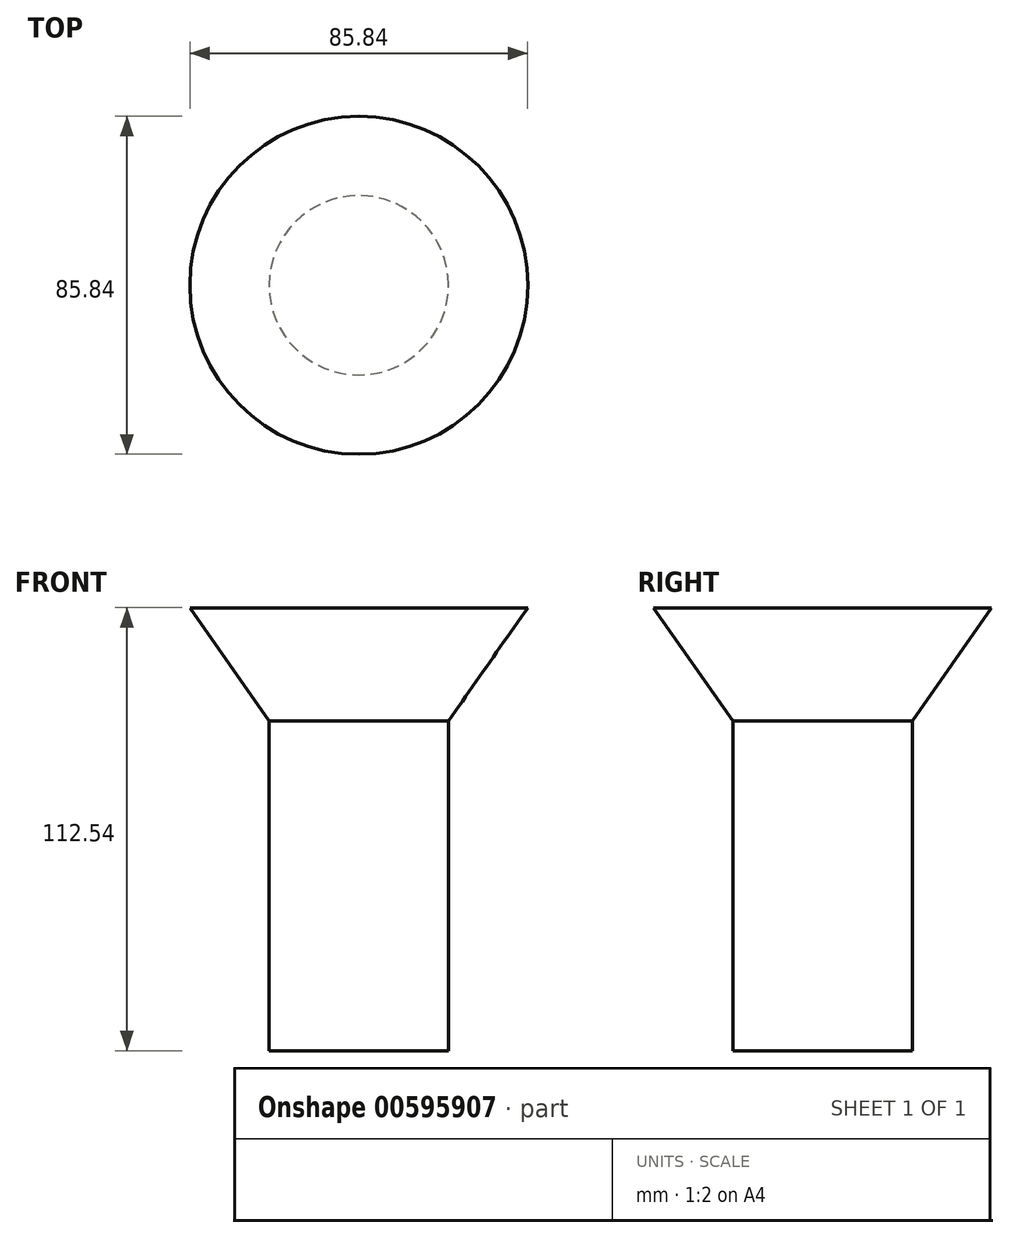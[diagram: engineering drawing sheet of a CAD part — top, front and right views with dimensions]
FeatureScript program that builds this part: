
annotation { "Feature Type Name" : "Feature", "Feature Type Description" : "" }
export const myFeature = defineFeature(function(context is Context, id is Id, definition is map)
    precondition{}
    {
        {
            var Q0;
            Q0=qCreatedBy(makeId("Right.planeOp"),FACE);
            var sketch = newSketch(context, id + "F0", { "sketchPlane" : qUnion([Q0])});
            skLineSegment(sketch, "E0", {"start": v(0, -50.31) * mm, "end": v(-22.8, -50.31) * mm});
            skLineSegment(sketch, "E1", {"start": v(-22.8, -50.31) * mm, "end": v(-22.8, 33.47) * mm});
            skLineSegment(sketch, "E2", {"start": v(-22.8, 33.47) * mm, "end": v(-42.92, 62.23) * mm});
            skLineSegment(sketch, "E3", {"start": v(-42.92, 62.23) * mm, "end": v(0, 62.23) * mm});
            skLineSegment(sketch, "E4", {"start": v(0, 62.23) * mm, "end": v(0, -50.31) * mm});
            skSolve(sketch);
        }
        {
            var Q0;
            Q0=makeQuery(id+"F0.imprint","IMPRINT",FACE,{"disambiguationData":[TD([[makeQuery(id+"F0.imprint","IMPRINT",EDGE,{"derivedFrom":sQuery(id+"F0.wireOp",EDGE,"E0")}),-1.0]])]});
            var Q1;
            Q1=sQuery(id+"F0.wireOp",EDGE,"E4");
            revolve(context, id + "F1", {"entities" : qUnion([Q0]), "axis" : qUnion([Q1]), "revolveType" : RevolveType.FULL});
        }
    });
